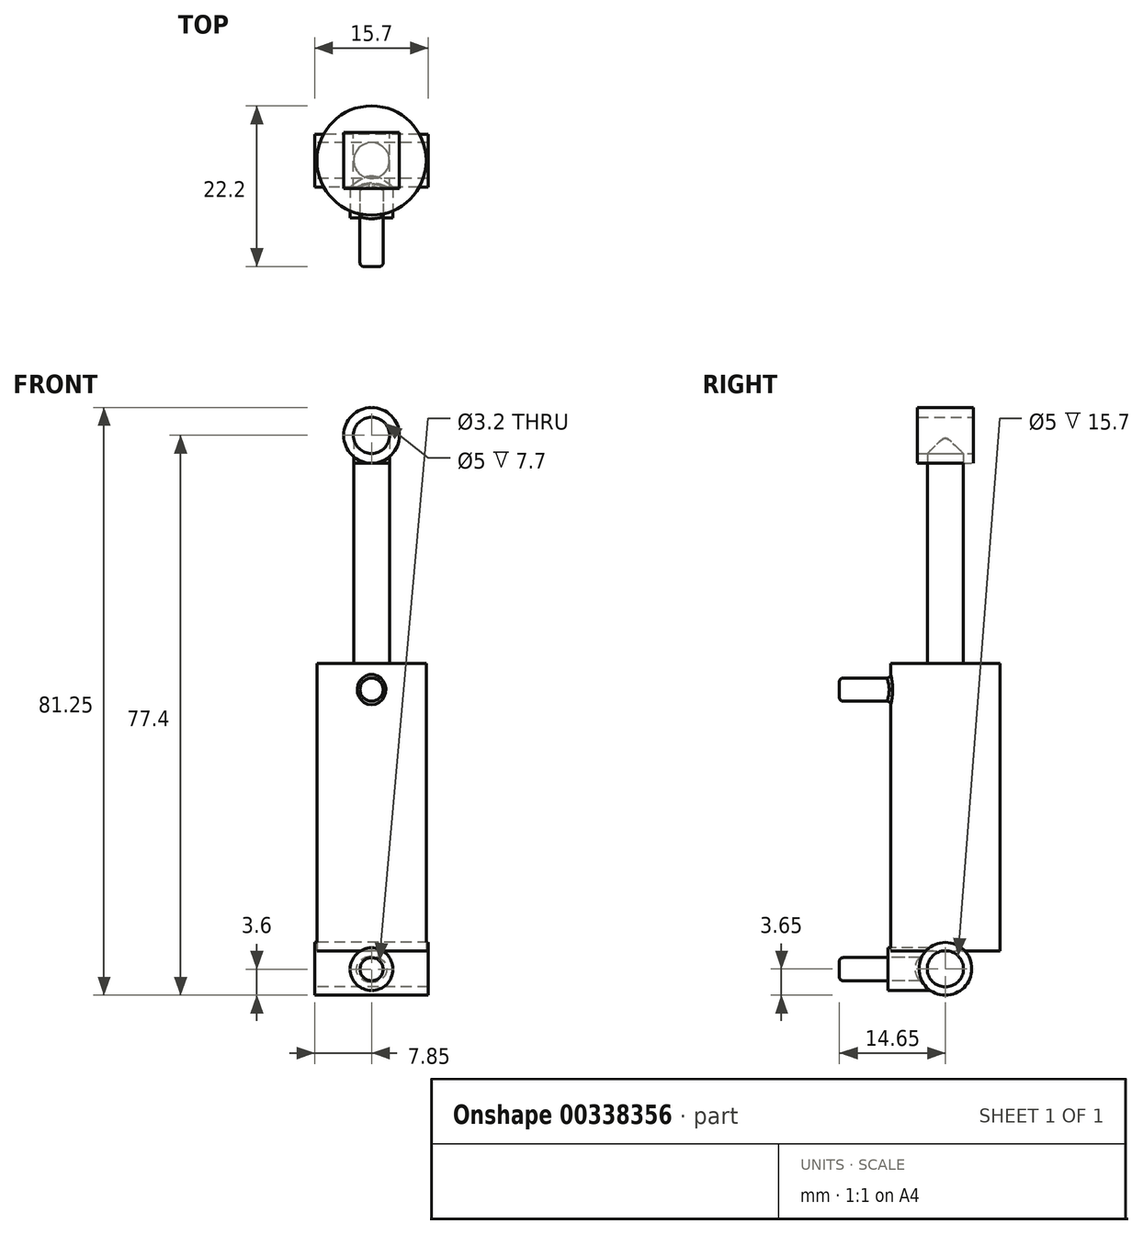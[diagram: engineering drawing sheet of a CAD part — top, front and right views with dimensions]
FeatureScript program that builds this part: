
annotation { "Feature Type Name" : "Feature", "Feature Type Description" : "" }
export const myFeature = defineFeature(function(context is Context, id is Id, definition is map)
    precondition{}
    {
        {
            var Q0;
            Q0=qCreatedBy(makeId("Top.planeOp"),FACE);
            var sketch = newSketch(context, id + "F0", { "sketchPlane" : qUnion([Q0])});
            skCircle(sketch, "E0", {"center": v(0, 0) * mm, "radius": 7.55 * mm});
            skSolve(sketch);
        }
        {
            var Q0;
            Q0 = qSketchRegion(id + "F0", true);
            extrude(context, id + "F1", {"entities" : qUnion([Q0]), "endBound" : BoundingType.SYMMETRIC, "depth" : 39.7 * mm});
        }
        {
            var Q0;
            Q0=makeQuery(id+"F1.opExtrude","CAP_FACE",FACE,{"disambiguationData":[OSD([sQuery(id+"F0.wireOp",EDGE,"E0")])],"isStart":false});
            var sketch = newSketch(context, id + "F2", { "sketchPlane" : qUnion([Q0])});
            skCircle(sketch, "E1", {"center": v(0, 0) * mm, "radius": 2.48 * mm});
            skSolve(sketch);
        }
        {
            var Q0;
            Q0 = qSketchRegion(id + "F2", true);
            extrude(context, id + "F3", {"entities" : qUnion([Q0]), "operationType" : NewBodyOperationType.ADD, "depth" : 27.7 * mm});
        }
        {
            var Q0;
            Q0=qCreatedBy(makeId("Front.planeOp"),FACE);
            var sketch = newSketch(context, id + "F4", { "sketchPlane" : qUnion([Q0])});
            skLineSegment(sketch, "E2.0", {"start": v(-2.48, 47.55) * mm, "end": v(2.48, 47.55) * mm});
            skPoint(sketch, "E3", {"position": v(0, 51.4) * mm});
            skPoint(sketch, "E3.positionSnap0", {"position": v(0, 47.55) * mm});
            skCircle(sketch, "E4", {"center": v(0, 51.4) * mm, "radius": 3.85 * mm});
            skCircle(sketch, "E5", {"center": v(0, 51.4) * mm, "radius": 2.5 * mm});
            skSolve(sketch);
        }
        {
            var Q0;
            Q0 = qSketchRegion(id + "F4", true);
            extrude(context, id + "F5", {"entities" : qUnion([Q0]), "endBound" : BoundingType.SYMMETRIC, "depth" : 7.7 * mm});
        }
        {
            var Q0;
            Q0=makeQuery(id+"F3.opExtrude","CAP_FACE",FACE,{"disambiguationData":[OSD([sQuery(id+"F2.wireOp",EDGE,"E1")])],"isStart":false});
            var sketch = newSketch(context, id + "F6", { "sketchPlane" : qUnion([Q0])});
            skCircle(sketch, "E6.0", {"center": v(0, 0) * mm, "radius": 2.48 * mm});
            skSolve(sketch);
        }
        {
            var Q0;
            Q0=makeQuery(id+"F6.imprint","IMPRINT",FACE,{"disambiguationData":[TD([[makeQuery(id+"F6.imprint","IMPRINT",EDGE,{"derivedFrom":sQuery(id+"F6.wireOp",EDGE,"E6.0")}),1.0]])]});
            var Q1;
            Q1=makeQuery(id+"F5.opExtrude","SWEPT_FACE",FACE,{"disambiguationData":[OSD([sQuery(id+"F4.wireOp",EDGE,"E5")])]});
            extrude(context, id + "F7", {"entities" : qUnion([Q0]), "endBound" : BoundingType.UP_TO_SURFACE, "endBoundEntityFace" : qUnion([Q1]), "depth" : 5 * mm});
        }
        {
            var Q0;
            Q0=qCreatedBy(makeId("Front.planeOp"),FACE);
            var Q1;
            Q1 = qBodyType(qCreatedBy(id + "F11" ,EDGE), BodyType.WIRE);
            cPlane(context, id + "F8", {"entities" : qUnion([Q0, Q1]), "cplaneType" : CPlaneType.OFFSET, "offset" : (15 / 2 + 7.15) * mm, "width" : 150 * mm, "height" : 150 * mm});
        }
        {
            var Q0;
            Q0=qCreatedBy(makeId("Right.planeOp"),FACE);
            var sketch = newSketch(context, id + "F9", { "sketchPlane" : qUnion([Q0])});
            skPoint(sketch, "E7", {"position": v(0, -22.35) * mm});
            skCircle(sketch, "E8", {"center": v(0, -22.35) * mm, "radius": 3.65 * mm});
            skCircle(sketch, "E9", {"center": v(0, -22.35) * mm, "radius": 2.5 * mm});
            skSolve(sketch);
        }
        {
            var Q0;
            Q0 = qSketchRegion(id + "F9", true);
            extrude(context, id + "F10", {"entities" : qUnion([Q0]), "endBound" : BoundingType.SYMMETRIC, "depth" : 15.7 * mm});
        }
        {
            var Q0;
            Q0=qCreatedBy(id+"F8.planeOp",FACE);
            var sketch = newSketch(context, id + "F11", { "sketchPlane" : qUnion([Q0])});
            skLineSegment(sketch, "E10", {"start": v(-7.55, -19.85) * mm, "end": v(-7.55, 19.85) * mm});
            skLineSegment(sketch, "E11", {"start": v(7.55, 19.85) * mm, "end": v(7.55, -19.85) * mm});
            skPoint(sketch, "E12", {"position": v(0, 16.25) * mm});
            skPoint(sketch, "E13", {"position": v(0, -22.4) * mm});
            skCircle(sketch, "E14", {"center": v(0, 16.25) * mm, "radius": 1.6 * mm});
            skLineSegment(sketch, "E15", {"start": v(7.85, -26) * mm, "end": v(-7.85, -26) * mm});
            skCircle(sketch, "E16", {"center": v(0, -22.4) * mm, "radius": 1.6 * mm});
            skCircle(sketch, "E17", {"center": v(0, -22.4) * mm, "radius": 2.93 * mm});
            skSolve(sketch);
        }
        {
            var Q0;
            Q0=makeQuery(id+"F11.imprint","IMPRINT",FACE,{"disambiguationData":[TD([[makeQuery(id+"F11.imprint","IMPRINT",EDGE,{"derivedFrom":sQuery(id+"F11.wireOp",EDGE,"E14")}),1.0]])]});
            var Q1;
            Q1=makeQuery(id+"F1.opExtrude","SWEPT_FACE",FACE,{"disambiguationData":[OSD([sQuery(id+"F0.wireOp",EDGE,"E0")])]});
            extrude(context, id + "F12", {"entities" : qUnion([Q0]), "operationType" : NewBodyOperationType.ADD, "endBound" : BoundingType.UP_TO_SURFACE, "oppositeDirection" : true, "endBoundEntityFace" : qUnion([Q1]), "depth" : 25 * mm});
        }
        {
            var Q0;
            Q0=makeQuery(id+"F11.imprint","IMPRINT",FACE,{"disambiguationData":[TD([[makeQuery(id+"F11.imprint","IMPRINT",EDGE,{"derivedFrom":sQuery(id+"F11.wireOp",EDGE,"E16")}),1.0]])]});
            var Q1;
            Q1=makeQuery(id+"F10.opExtrude","SWEPT_FACE",FACE,{"disambiguationData":[OSD([sQuery(id+"F9.wireOp",EDGE,"E8")])]});
            extrude(context, id + "F13", {"entities" : qUnion([Q0]), "operationType" : NewBodyOperationType.ADD, "endBound" : BoundingType.UP_TO_SURFACE, "oppositeDirection" : true, "endBoundEntityFace" : qUnion([Q1]), "depth" : 25 * mm});
        }
        {
            var Q0;
            Q0=makeQuery(id+"F13.opExtrude","CAP_FACE",FACE,{"disambiguationData":[OSD([sQuery(id+"F11.wireOp",EDGE,"E16")])],"isStart":true});
            cPlane(context, id + "F14", {"entities" : qUnion([Q0]), "cplaneType" : CPlaneType.OFFSET, "offset" : 6.7 * mm, "oppositeDirection" : true, "width" : 150 * mm, "height" : 150 * mm});
        }
        {
            var Q0;
            Q0=qCreatedBy(id+"F14.planeOp",FACE);
            var sketch = newSketch(context, id + "F15", { "sketchPlane" : qUnion([Q0])});
            skCircle(sketch, "E18.0.0", {"center": v(0, -22.4) * mm, "radius": 1.6 * mm});
            skCircle(sketch, "E19", {"center": v(0, -22.4) * mm, "radius": 2.95 * mm});
            skSolve(sketch);
        }
        {
            var Q0;
            Q0 = qSketchRegion(id + "F15", true);
            var Q1;
            Q1=makeQuery(id+"F10.opExtrude","SWEPT_FACE",FACE,{"disambiguationData":[OSD([sQuery(id+"F9.wireOp",EDGE,"E8")])]});
            extrude(context, id + "F16", {"entities" : qUnion([Q0]), "endBound" : BoundingType.UP_TO_SURFACE, "oppositeDirection" : true, "endBoundEntityFace" : qUnion([Q1]), "depth" : 25 * mm});
        }
        {
            var Q0;
            Q0=makeQuery(id+"F13.opExtrude","SWEPT_FACE",FACE,{"disambiguationData":[OSD([sQuery(id+"F11.wireOp",EDGE,"E16")])]});
            var Q1;
            Q1=makeQuery(id+"F13.opExtrude","CAP_FACE",FACE,{"disambiguationData":[OSD([sQuery(id+"F11.wireOp",EDGE,"E16")])],"isStart":true});
            var Q2;
            Q2=makeQuery(id+"F12.opExtrude","SWEPT_FACE",FACE,{"disambiguationData":[OSD([sQuery(id+"F11.wireOp",EDGE,"E14")])]});
            var Q3;
            Q3=makeQuery(id+"F12.opExtrude","CAP_FACE",FACE,{"disambiguationData":[OSD([sQuery(id+"F11.wireOp",EDGE,"E14")])],"isStart":true});
            fillet(context, id + "F17", {"entities" : qUnion([Q0, Q1, Q2, Q3]), "radius" : 0.5 * mm, "tangentPropagation" : true, "allowEdgeOverflow" : false});
        }
    });
